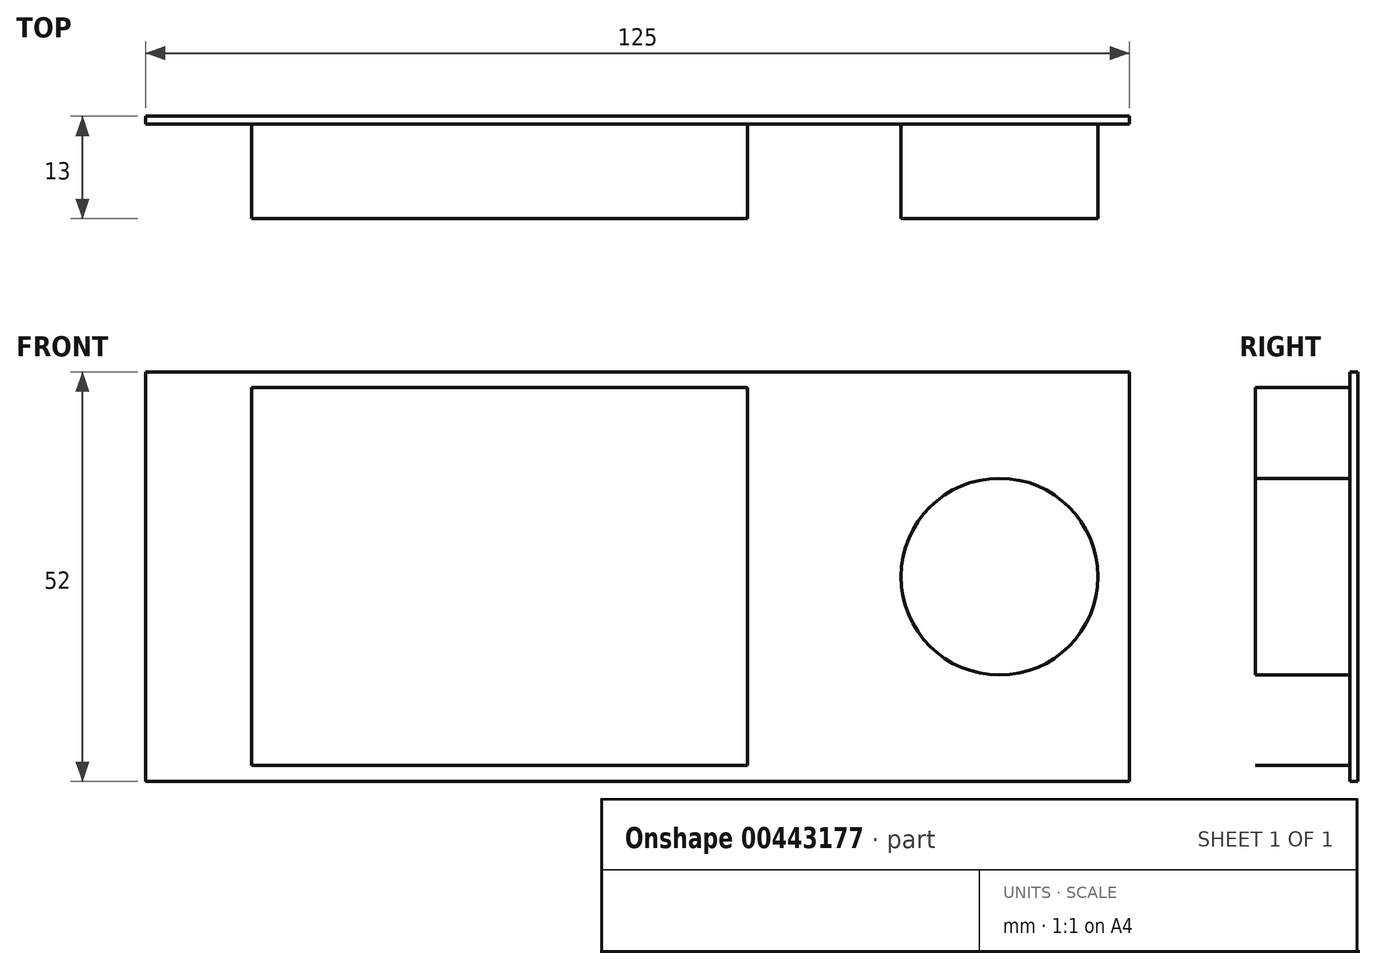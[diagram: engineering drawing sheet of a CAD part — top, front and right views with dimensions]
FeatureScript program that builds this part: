
annotation { "Feature Type Name" : "Feature", "Feature Type Description" : "" }
export const myFeature = defineFeature(function(context is Context, id is Id, definition is map)
    precondition{}
    {
        {
            var Q0;
            Q0=qCreatedBy(makeId("Front.planeOp"),FACE);
            var sketch = newSketch(context, id + "F0", { "sketchPlane" : qUnion([Q0])});
            skLineSegment(sketch, "E0.bottom", {"start": v(62.5, 26) * mm, "end": v(-62.5, 26) * mm});
            skLineSegment(sketch, "E0.top", {"start": v(62.5, -26) * mm, "end": v(-62.5, -26) * mm});
            skLineSegment(sketch, "E0.left", {"start": v(62.5, 26) * mm, "end": v(62.5, -26) * mm});
            skLineSegment(sketch, "E0.right", {"start": v(-62.5, 26) * mm, "end": v(-62.5, -26) * mm});
            skPoint(sketch, "E0.middle", {"position": v(0, 0) * mm});
            skCircle(sketch, "E1", {"center": v(46, 0) * mm, "radius": 12.5 * mm});
            skLineSegment(sketch, "E2.bottom", {"start": v(14, 24) * mm, "end": v(-49, 24) * mm});
            skLineSegment(sketch, "E2.top", {"start": v(14, -24) * mm, "end": v(-49, -24) * mm});
            skLineSegment(sketch, "E2.left", {"start": v(14, 24) * mm, "end": v(14, -24) * mm});
            skLineSegment(sketch, "E2.right", {"start": v(-49, 24) * mm, "end": v(-49, -24) * mm});
            skPoint(sketch, "E2.middle", {"position": v(-17.5, 0) * mm});
            skSolve(sketch);
        }
        {
            var Q0;
            Q0 = qSketchRegion(id + "F0", true);
            var Q1;
            Q1=makeQuery(id+"F0.imprint","IMPRINT",FACE,{"disambiguationData":[TD([[makeQuery(id+"F0.imprint","IMPRINT",EDGE,{"derivedFrom":sQuery(id+"F0.wireOp",EDGE,"E2.bottom")}),1.0]])]});
            var Q2;
            Q2=makeQuery(id+"F0.imprint","IMPRINT",FACE,{"disambiguationData":[TD([[makeQuery(id+"F0.imprint","IMPRINT",EDGE,{"derivedFrom":sQuery(id+"F0.wireOp",EDGE,"E1")}),1.0]])]});
            extrude(context, id + "F1", {"entities" : qUnion([Q0, Q1, Q2]), "oppositeDirection" : true, "depth" : 1 * mm});
        }
        {
            var Q0;
            Q0=makeQuery(id+"F0.imprint","IMPRINT",FACE,{"disambiguationData":[TD([[makeQuery(id+"F0.imprint","IMPRINT",EDGE,{"derivedFrom":sQuery(id+"F0.wireOp",EDGE,"E2.bottom")}),1.0]])]});
            var Q1;
            Q1=makeQuery(id+"F0.imprint","IMPRINT",FACE,{"disambiguationData":[TD([[makeQuery(id+"F0.imprint","IMPRINT",EDGE,{"derivedFrom":sQuery(id+"F0.wireOp",EDGE,"E1")}),1.0]])]});
            extrude(context, id + "F2", {"entities" : qUnion([Q0, Q1]), "operationType" : NewBodyOperationType.ADD, "depth" : 12 * mm});
        }
    });
